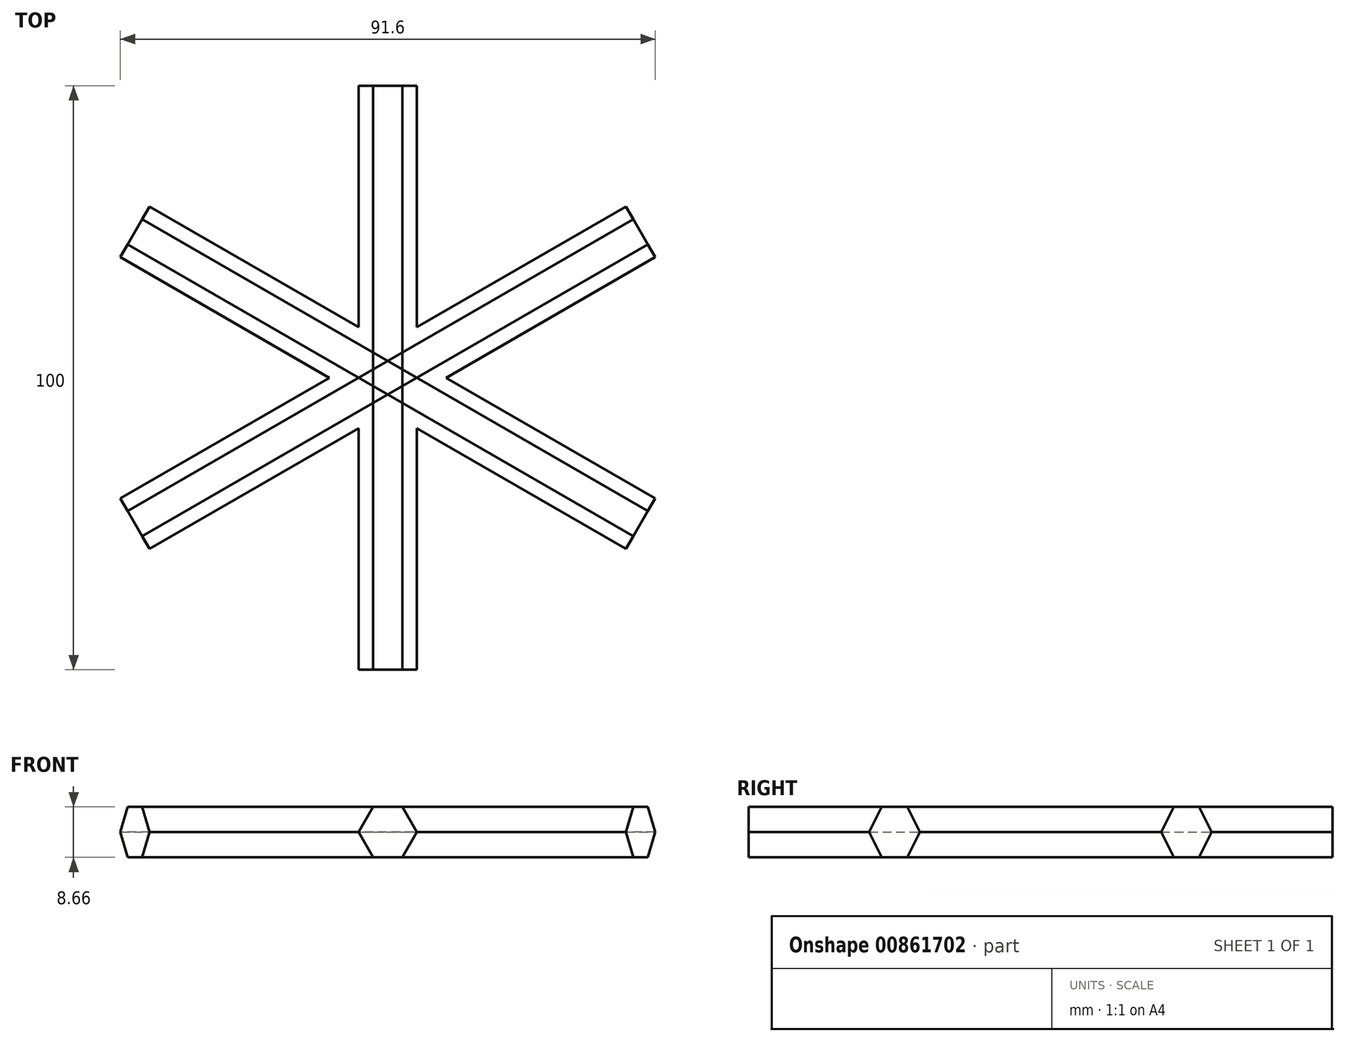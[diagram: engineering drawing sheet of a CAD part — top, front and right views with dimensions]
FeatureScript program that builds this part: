
annotation { "Feature Type Name" : "Feature", "Feature Type Description" : "" }
export const myFeature = defineFeature(function(context is Context, id is Id, definition is map)
    precondition{}
    {
        {
            var Q0;
            Q0=qCreatedBy(makeId("Top.planeOp"),FACE);
            var sketch = newSketch(context, id + "F0", { "sketchPlane" : qUnion([Q0])});
            skCircle(sketch, "E0", {"center": v(0, 0) * mm, "radius": 50 * mm, "construction": true});
            skCircle(sketch, "E1", {"center": v(0, 0) * mm, "radius": 5 * mm});
            skLineSegment(sketch, "E2", {"start": v(-70.9, 0) * mm, "end": v(69.7, 0) * mm, "construction": true});
            skLineSegment(sketch, "E3", {"start": v(0, 70.66) * mm, "end": v(0, -68.48) * mm, "construction": true});
            skCircle(sketch, "E4.cCircle", {"center": v(0, 0) * mm, "radius": 5 * mm, "construction": true});
            skLineSegment(sketch, "E4.0", {"start": v(5, 0) * mm, "end": v(2.5, -4.33) * mm});
            skLineSegment(sketch, "E4.1", {"start": v(2.5, -4.33) * mm, "end": v(-2.5, -4.33) * mm});
            skLineSegment(sketch, "E4.2", {"start": v(-2.5, -4.33) * mm, "end": v(-5, 0) * mm});
            skLineSegment(sketch, "E4.3", {"start": v(-5, 0) * mm, "end": v(-2.5, 4.33) * mm});
            skLineSegment(sketch, "E4.4", {"start": v(-2.5, 4.33) * mm, "end": v(2.5, 4.33) * mm});
            skLineSegment(sketch, "E4.5", {"start": v(2.5, 4.33) * mm, "end": v(5, 0) * mm});
            skSolve(sketch);
        }
        {
            var Q0;
            Q0=makeQuery(id+"F0.imprint","IMPRINT",FACE,{"disambiguationData":[TD([[makeQuery(id+"F0.imprint","IMPRINT",EDGE,{"derivedFrom":sQuery(id+"F0.wireOp",EDGE,"E4.0")}),-1.0]])]});
            extrude(context, id + "F1", {"entities" : qUnion([Q0]), "endBound" : BoundingType.SYMMETRIC, "depth" : 100 * mm, "offsetDistance" : 25 * mm});
        }
        {
            var Q0;
            Q0=qCreatedBy(makeId("Front.planeOp"),FACE);
            var sketch = newSketch(context, id + "F2", { "sketchPlane" : qUnion([Q0])});
            skLineSegment(sketch, "E5", {"start": v(0, 73.56) * mm, "end": v(0, -62.44) * mm, "construction": true});
            skSolve(sketch);
        }
        {
            var Q0;
            Q0=qCreatedBy(makeId("Right.planeOp"),FACE);
            var sketch = newSketch(context, id + "F3", { "sketchPlane" : qUnion([Q0])});
            skCircle(sketch, "E6", {"center": v(49.96, 0) * mm, "radius": 5 * mm});
            skSolve(sketch);
        }
        {
            var Q0;
            Q0=makeQuery(id+"F1.opExtrude","SWEPT_BODY",BODY,{"disambiguationData":[OSD([sQuery(id+"F0.wireOp",EDGE,"pzFQj8xv-GmE5-ZWky-9ZE1-7gHvdMMdsQLE")])]});
            var Q1;
            Q1=makeQuery(id+"F1.opExtrude","SWEPT_BODY",BODY,{"disambiguationData":[OSD([sQuery(id+"F0.wireOp",EDGE,"E1")])]});
            var Q2;
            Q2=makeQuery(id+"F1.opExtrude","SWEPT_BODY",BODY,{"disambiguationData":[OSD([sQuery(id+"F0.wireOp",EDGE,"E4.0"),sQuery(id+"F0.wireOp",EDGE,"E4.1"),sQuery(id+"F0.wireOp",EDGE,"E4.2"),sQuery(id+"F0.wireOp",EDGE,"E4.3"),sQuery(id+"F0.wireOp",EDGE,"E4.4"),sQuery(id+"F0.wireOp",EDGE,"E4.5")])]});
            var Q3;
            Q3=sQuery(id+"F0.wireOp",EDGE,"E2");
            transform(context, id + "F4", {"entities" : qUnion([Q0, Q1, Q2]), "transformType" : TransformType.ROTATION, "transformAxis" : qUnion([Q3]), "angle" : 90 * degree, "makeCopy" : false});
        }
        {
            var Q0;
            Q0=makeQuery(id+"F1.opExtrude","SWEPT_BODY",BODY,{"disambiguationData":[OSD([sQuery(id+"F0.wireOp",EDGE,"E1")])]});
            var Q1;
            Q1=makeQuery(id+"F1.opExtrude","SWEPT_BODY",BODY,{"disambiguationData":[OSD([sQuery(id+"F0.wireOp",EDGE,"E4.0"),sQuery(id+"F0.wireOp",EDGE,"E4.1"),sQuery(id+"F0.wireOp",EDGE,"E4.2"),sQuery(id+"F0.wireOp",EDGE,"E4.3"),sQuery(id+"F0.wireOp",EDGE,"E4.4"),sQuery(id+"F0.wireOp",EDGE,"E4.5")])]});
            var Q2;
            Q2=sQuery(id+"F2.wireOp",EDGE,"E5");
            circularPattern(context, id + "F5", {"entities" : qUnion([Q0, Q1]), "axis" : qUnion([Q2]), "angle" : 360 * degree, "instanceCount" : 6, "equalSpace" : true});
        }
        {
            var Q0;
            Q0=sQuery(id+"F3.wireOp",EDGE,"E6");
            var Q1;
            Q1=sQuery(id+"F2.wireOp",EDGE,"E5");
            revolve(context, id + "F6", {"bodyType" : ToolBodyType.SURFACE, "surfaceOperationType" : NewSurfaceOperationType.NEW, "surfaceEntities" : qUnion([Q0]), "axis" : qUnion([Q1]), "revolveType" : RevolveType.FULL});
        }
    });
